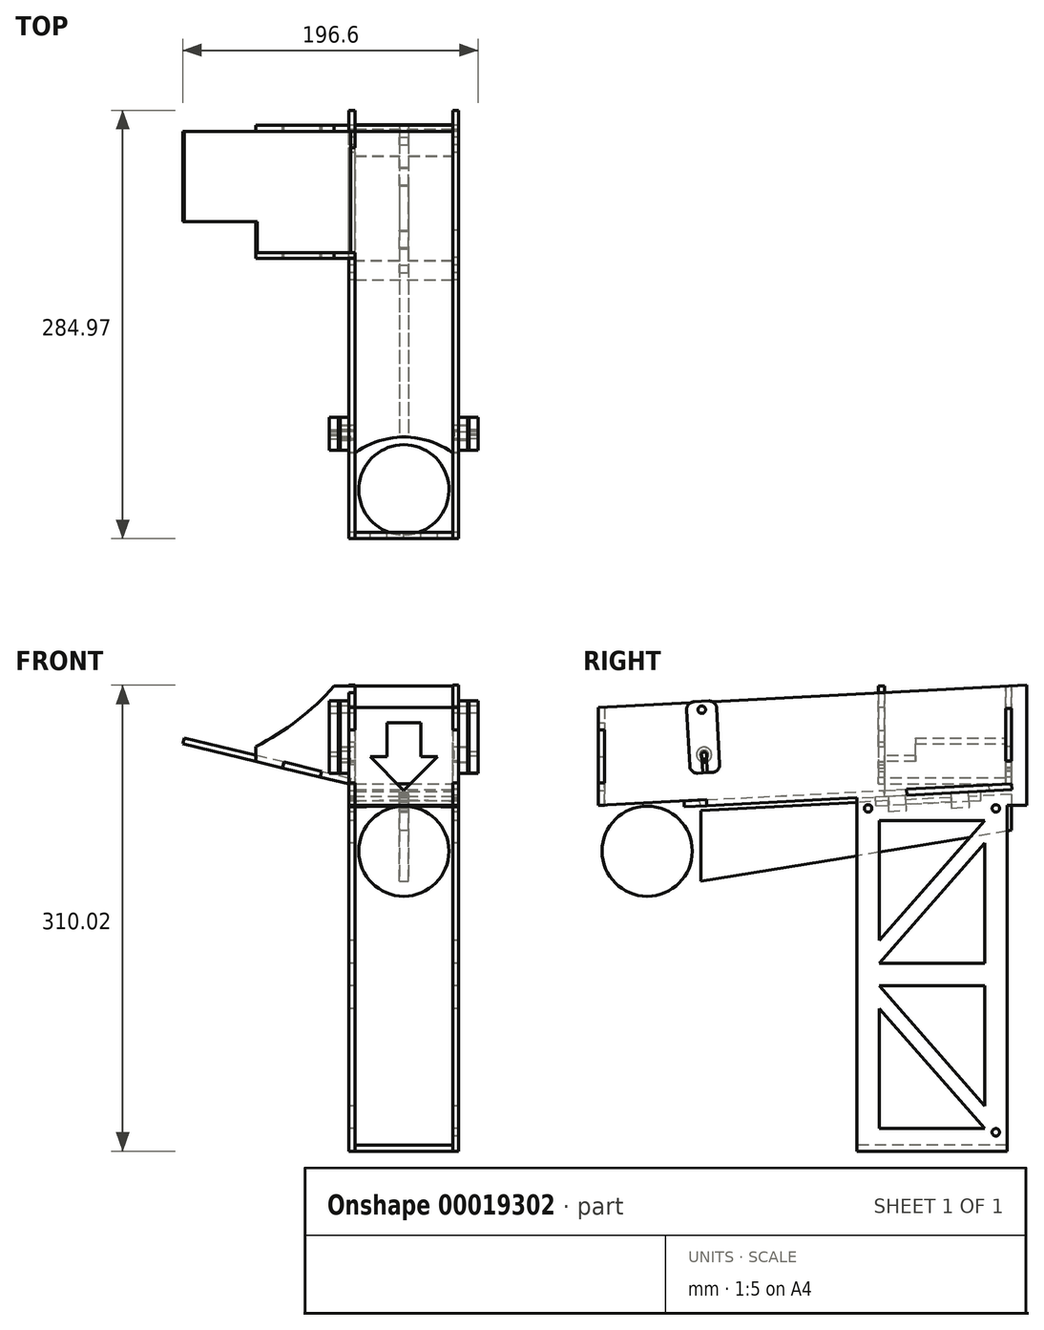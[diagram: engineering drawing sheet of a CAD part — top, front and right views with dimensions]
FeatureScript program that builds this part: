
annotation { "Feature Type Name" : "Feature", "Feature Type Description" : "" }
export const myFeature = defineFeature(function(context is Context, id is Id, definition is map)
    precondition{}
    {
        {
            var Q0;
            Q0=qCreatedBy(makeId("Right.planeOp"),FACE);
            var sketch = newSketch(context, id + "F0", { "sketchPlane" : qUnion([Q0])});
            skLineSegment(sketch, "E0", {"start": v(0, 0) * mm, "end": v(71.9, 3.77) * mm});
            skLineSegment(sketch, "E1", {"start": v(274.97, 79.5) * mm, "end": v(0, 65.09) * mm});
            skLineSegment(sketch, "E2", {"start": v(0, 65.09) * mm, "end": v(0, 50.09) * mm});
            skLineSegment(sketch, "E3.top", {"start": v(71.9, 0) * mm, "end": v(0, 0) * mm, "construction": true});
            skPoint(sketch, "E4.orphan", {"position": v(274.97, 14.41) * mm});
            skLineSegment(sketch, "E5", {"start": v(274.97, 14.41) * mm, "end": v(275.18, 10.42) * mm, "construction": true});
            skLineSegment(sketch, "E6", {"start": v(274.97, 79.5) * mm, "end": v(274.97, 14.41) * mm, "construction": true});
            skLineSegment(sketch, "E7", {"start": v(275.18, 10.42) * mm, "end": v(274.97, 14.41) * mm});
            skLineSegment(sketch, "E8", {"start": v(205.07, 10.75) * mm, "end": v(205.28, 6.75) * mm});
            skLineSegment(sketch, "E9", {"start": v(205.28, 6.75) * mm, "end": v(275.18, 10.42) * mm});
            skLineSegment(sketch, "E10.bottom", {"start": v(274.97, 64.5) * mm, "end": v(270.97, 64.5) * mm});
            skLineSegment(sketch, "E10.top", {"start": v(274.97, 29.5) * mm, "end": v(270.97, 29.5) * mm});
            skLineSegment(sketch, "E10.left", {"start": v(274.97, 64.5) * mm, "end": v(274.97, 29.5) * mm});
            skLineSegment(sketch, "E10.right", {"start": v(270.97, 64.5) * mm, "end": v(270.97, 29.5) * mm});
            skLineSegment(sketch, "E11", {"start": v(205.07, 10.75) * mm, "end": v(274.97, 14.41) * mm});
            skLineSegment(sketch, "E12", {"start": v(72.11, -0.23) * mm, "end": v(171.97, 5) * mm});
            skLineSegment(sketch, "E13", {"start": v(71.9, 3.77) * mm, "end": v(72.11, -0.23) * mm});
            skLineSegment(sketch, "E14.bottom", {"start": v(0, 50.09) * mm, "end": v(4, 50.09) * mm});
            skLineSegment(sketch, "E14.top", {"start": v(0, 15.09) * mm, "end": v(4, 15.09) * mm});
            skLineSegment(sketch, "E14.right", {"start": v(4, 50.09) * mm, "end": v(4, 15.09) * mm});
            skLineSegment(sketch, "E15.trimOffspring", {"start": v(0, 15.09) * mm, "end": v(0, 0) * mm});
            skLineSegment(sketch, "E16", {"start": v(171.97, 5) * mm, "end": v(171.97, -230) * mm});
            skLineSegment(sketch, "E17", {"start": v(171.97, -230) * mm, "end": v(271.97, -230) * mm});
            skLineSegment(sketch, "E18", {"start": v(284.97, 0) * mm, "end": v(284.97, 80.02) * mm});
            skLineSegment(sketch, "E19", {"start": v(284.97, 80.02) * mm, "end": v(274.97, 79.5) * mm});
            skLineSegment(sketch, "E20", {"start": v(284.97, 0) * mm, "end": v(271.97, 0) * mm});
            skLineSegment(sketch, "E21", {"start": v(271.97, 0) * mm, "end": v(271.97, -230) * mm});
            skLineSegment(sketch, "E22", {"start": v(186.97, -10) * mm, "end": v(256.97, -10) * mm});
            skLineSegment(sketch, "E23", {"start": v(256.97, -10) * mm, "end": v(186.97, -89.83) * mm});
            skLineSegment(sketch, "E24", {"start": v(186.97, -89.83) * mm, "end": v(186.97, -10) * mm});
            skLineSegment(sketch, "E25", {"start": v(186.97, -105) * mm, "end": v(256.97, -25.16) * mm});
            skLineSegment(sketch, "E26", {"start": v(256.97, -25.16) * mm, "end": v(256.97, -105) * mm});
            skLineSegment(sketch, "E27", {"start": v(256.97, -105) * mm, "end": v(186.97, -105) * mm});
            skLineSegment(sketch, "E28", {"start": v(186.97, -120) * mm, "end": v(256.97, -199.83) * mm});
            skLineSegment(sketch, "E29", {"start": v(256.97, -199.83) * mm, "end": v(256.97, -120) * mm});
            skLineSegment(sketch, "E30", {"start": v(256.97, -120) * mm, "end": v(186.97, -120) * mm});
            skLineSegment(sketch, "E31", {"start": v(186.97, -135.16) * mm, "end": v(256.97, -215) * mm});
            skLineSegment(sketch, "E32", {"start": v(256.97, -215) * mm, "end": v(186.97, -215) * mm});
            skLineSegment(sketch, "E33", {"start": v(186.97, -215) * mm, "end": v(186.97, -135.16) * mm});
            skCircle(sketch, "E34", {"center": v(70.33, 33.73) * mm, "radius": 5 * mm});
            skLineSegment(sketch, "E35", {"start": v(70.33, 33.73) * mm, "end": v(68.5, 68.68) * mm, "construction": true});
            skCircle(sketch, "E36", {"center": v(68.76, 63.69) * mm, "radius": 2.5 * mm});
            skCircle(sketch, "E37", {"center": v(179.47, -2) * mm, "radius": 2.5 * mm});
            skCircle(sketch, "E38", {"center": v(264.47, -2) * mm, "radius": 2.5 * mm});
            skCircle(sketch, "E39", {"center": v(264.47, -217.45) * mm, "radius": 2.5 * mm});
            skSolve(sketch);
        }
        {
            var Q0;
            Q0=qSketchRegion(id+"F0",true);
            extrude(context, id + "F1", {"entities" : qUnion([Q0]), "depth" : 4 * mm});
        }
        {
            var Q0;
            Q0=makeQuery(id+"F1.opExtrude","SWEPT_FACE",FACE,{"disambiguationData":[OSD([sQuery(id+"F0.wireOp",EDGE,"E0")])]});
            var sketch = newSketch(context, id + "F2", { "sketchPlane" : qUnion([Q0])});
            skLineSegment(sketch, "E40.top", {"start": v(4, -275.35) * mm, "end": v(0, -275.35) * mm});
            skLineSegment(sketch, "E40.left", {"start": v(4, -57) * mm, "end": v(4, -72) * mm});
            skLineSegment(sketch, "E40.right", {"start": v(-69, -57) * mm, "end": v(-69, -72) * mm});
            skLineSegment(sketch, "E41", {"start": v(4, -57) * mm, "end": v(0, -57) * mm});
            skLineSegment(sketch, "E42", {"start": v(-65, -275.35) * mm, "end": v(0, -275.35) * mm});
            skLineSegment(sketch, "E43", {"start": v(0, -72) * mm, "end": v(0, -205.35) * mm});
            skLineSegment(sketch, "E44.0", {"start": v(4, -72) * mm, "end": v(0, -72) * mm});
            skLineSegment(sketch, "E45.0", {"start": v(4, -205.35) * mm, "end": v(0, -205.35) * mm});
            skLineSegment(sketch, "E46", {"start": v(4, -205.35) * mm, "end": v(4, -275.35) * mm});
            skLineSegment(sketch, "E47", {"start": v(0, -275.35) * mm, "end": v(4, -275.35) * mm});
            skLineSegment(sketch, "E48.bottom", {"start": v(-69, -260.35) * mm, "end": v(-65, -260.35) * mm});
            skLineSegment(sketch, "E48.top", {"start": v(-69, -190.35) * mm, "end": v(-65, -190.35) * mm});
            skLineSegment(sketch, "E49", {"start": v(-65, -260.35) * mm, "end": v(-65, -275.35) * mm});
            skLineSegment(sketch, "E50", {"start": v(-69, -72) * mm, "end": v(-65, -72) * mm});
            skLineSegment(sketch, "E51", {"start": v(-65, -72) * mm, "end": v(-65, -190.35) * mm});
            skLineSegment(sketch, "E52.trimOffspring", {"start": v(-69, -190.35) * mm, "end": v(-69, -260.35) * mm});
            skArc(sketch, "E53", {"start": v(-65, -57) * mm, "mid": v(-32.5, -67.63) * mm, "end": v(0, -57) * mm});
            skLineSegment(sketch, "E54", {"start": v(-32.5, -57) * mm, "end": v(-32.5, -275.35) * mm, "construction": true});
            skLineSegment(sketch, "E55.trimOffspring", {"start": v(-65, -57) * mm, "end": v(-69, -57) * mm});
            skCircle(sketch, "E56", {"center": v(-32.5, -32.2) * mm, "radius": 30 * mm, "construction": true});
            skLineSegment(sketch, "E57", {"start": v(0, 0) * mm, "end": v(-69, 0) * mm, "construction": true});
            skLineSegment(sketch, "E58", {"start": v(-65, -57) * mm, "end": v(-65, 0) * mm, "construction": true});
            skSolve(sketch);
        }
        {
            var Q0;
            Q0=qSketchRegion(id+"F2",true);
            extrude(context, id + "F3", {"entities" : qUnion([Q0]), "depth" : 4 * mm});
        }
        {
            var Q0;
            Q0=makeQuery(id+"F3.opExtrude","SWEPT_FACE",FACE,{"disambiguationData":[OSD([sQuery(id+"F2.wireOp",EDGE,"E40.right")])]});
            var sketch = newSketch(context, id + "F4", { "sketchPlane" : qUnion([Q0])});
            skPoint(sketch, "E59.0.2.start.orphan", {"position": v(0, 65.09) * mm});
            skLineSegment(sketch, "E60.1", {"start": v(-274.97, 64.5) * mm, "end": v(-274.97, 29.5) * mm});
            skLineSegment(sketch, "E60.2", {"start": v(-274.97, 64.5) * mm, "end": v(-270.97, 64.5) * mm});
            skLineSegment(sketch, "E60.4", {"start": v(-274.97, 29.5) * mm, "end": v(-270.97, 29.5) * mm});
            skLineSegment(sketch, "E60.11", {"start": v(-190.3, 5.97) * mm, "end": v(-260.2, 9.63) * mm});
            skLineSegment(sketch, "E60.12", {"start": v(-260.2, 9.63) * mm, "end": v(-260, 13.63) * mm});
            skLineSegment(sketch, "E60.14", {"start": v(-190.3, 9.97) * mm, "end": v(-190.3, 5.97) * mm});
            skLineSegment(sketch, "E60.26", {"start": v(-72.11, -0.23) * mm, "end": v(-171.97, 5) * mm});
            skLineSegment(sketch, "E60.27", {"start": v(-71.9, 3.77) * mm, "end": v(-72.11, -0.23) * mm});
            skLineSegment(sketch, "E60.28", {"start": v(0, 0) * mm, "end": v(-71.9, 3.77) * mm});
            skLineSegment(sketch, "E60.29", {"start": v(0, 65.09) * mm, "end": v(0, 50.09) * mm});
            skLineSegment(sketch, "E61", {"start": v(-270.97, 64.5) * mm, "end": v(-270.97, 79.3) * mm});
            skLineSegment(sketch, "E62", {"start": v(-270.97, 29.5) * mm, "end": v(-270.97, 14.2) * mm});
            skLineSegment(sketch, "E63", {"start": v(-270.97, 14.2) * mm, "end": v(-260, 13.63) * mm});
            skLineSegment(sketch, "E64", {"start": v(-190.3, 75.06) * mm, "end": v(-190.3, 65.06) * mm});
            skLineSegment(sketch, "E65", {"start": v(0, 50.09) * mm, "end": v(-4, 50.09) * mm});
            skLineSegment(sketch, "E66", {"start": v(-4, 50.09) * mm, "end": v(-4, 15.09) * mm});
            skLineSegment(sketch, "E67", {"start": v(-4, 15.09) * mm, "end": v(0, 15.09) * mm});
            skLineSegment(sketch, "E68.trimOffspring", {"start": v(0, 15.09) * mm, "end": v(0, 0) * mm});
            skLineSegment(sketch, "E69.trimOffspring", {"start": v(0, 50.09) * mm, "end": v(0, 65.09) * mm});
            skPoint(sketch, "E59.0.0.start.orphan", {"position": v(0, 50.09) * mm});
            skLineSegment(sketch, "E70", {"start": v(-190.3, 65.06) * mm, "end": v(-186.3, 65.06) * mm});
            skLineSegment(sketch, "E71", {"start": v(-186.3, 65.06) * mm, "end": v(-186.3, 50.06) * mm});
            skLineSegment(sketch, "E72", {"start": v(-186.3, 50.06) * mm, "end": v(-190.3, 50.06) * mm});
            skLineSegment(sketch, "E73", {"start": v(-190.3, 42.06) * mm, "end": v(-186.3, 42.06) * mm});
            skLineSegment(sketch, "E74", {"start": v(-186.3, 42.06) * mm, "end": v(-186.3, 27.06) * mm});
            skLineSegment(sketch, "E75", {"start": v(-186.3, 27.06) * mm, "end": v(-190.3, 27.06) * mm});
            skLineSegment(sketch, "E76.trimOffspring", {"start": v(-190.3, 50.06) * mm, "end": v(-190.3, 42.06) * mm});
            skLineSegment(sketch, "E77.trimOffspring", {"start": v(-190.3, 27.06) * mm, "end": v(-190.3, 9.97) * mm});
            skLineSegment(sketch, "E78", {"start": v(-171.97, 5) * mm, "end": v(-171.97, -230) * mm});
            skLineSegment(sketch, "E79", {"start": v(-171.97, -230) * mm, "end": v(-271.97, -230) * mm});
            skLineSegment(sketch, "E80", {"start": v(-284.97, 0) * mm, "end": v(-284.97, 80.02) * mm});
            skLineSegment(sketch, "E81", {"start": v(-270.97, 79.3) * mm, "end": v(-284.97, 80.02) * mm});
            skLineSegment(sketch, "E82", {"start": v(0, 65.09) * mm, "end": v(-190.3, 75.06) * mm});
            skLineSegment(sketch, "E83", {"start": v(-271.97, 0) * mm, "end": v(-284.97, 0) * mm});
            skLineSegment(sketch, "E84.0", {"start": v(-186.97, -10) * mm, "end": v(-256.97, -10) * mm});
            skLineSegment(sketch, "E85.0", {"start": v(-186.97, -89.83) * mm, "end": v(-186.97, -10) * mm});
            skLineSegment(sketch, "E86.0", {"start": v(-256.97, -10) * mm, "end": v(-186.97, -89.83) * mm});
            skLineSegment(sketch, "E87.0", {"start": v(-186.97, -105) * mm, "end": v(-256.97, -25.16) * mm});
            skLineSegment(sketch, "E88.0", {"start": v(-256.97, -25.16) * mm, "end": v(-256.97, -105) * mm});
            skLineSegment(sketch, "E89.0", {"start": v(-256.97, -105) * mm, "end": v(-186.97, -105) * mm});
            skLineSegment(sketch, "E90.0", {"start": v(-256.97, -120) * mm, "end": v(-186.97, -120) * mm});
            skLineSegment(sketch, "E91.0", {"start": v(-256.97, -199.83) * mm, "end": v(-256.97, -120) * mm});
            skLineSegment(sketch, "E92.0", {"start": v(-186.97, -120) * mm, "end": v(-256.97, -199.83) * mm});
            skLineSegment(sketch, "E93.0", {"start": v(-186.97, -135.16) * mm, "end": v(-256.97, -215) * mm});
            skLineSegment(sketch, "E94.0", {"start": v(-186.97, -215) * mm, "end": v(-186.97, -135.16) * mm});
            skLineSegment(sketch, "E95.0", {"start": v(-256.97, -215) * mm, "end": v(-186.97, -215) * mm});
            skLineSegment(sketch, "E96", {"start": v(-271.97, -230) * mm, "end": v(-271.97, 0) * mm});
            skCircle(sketch, "E97.0", {"center": v(-70.33, 33.73) * mm, "radius": 5 * mm});
            skCircle(sketch, "E98.0", {"center": v(-68.76, 63.69) * mm, "radius": 2.5 * mm});
            skCircle(sketch, "E99.0", {"center": v(-179.47, -2) * mm, "radius": 2.5 * mm});
            skCircle(sketch, "E99.1", {"center": v(-264.47, -2) * mm, "radius": 2.5 * mm});
            skSolve(sketch);
        }
        {
            var Q0;
            Q0=qSketchRegion(id+"F4",true);
            extrude(context, id + "F5", {"entities" : qUnion([Q0]), "oppositeDirection" : true, "depth" : 4 * mm});
        }
        {
            var Q0;
            Q0=makeQuery(id+"F5.opExtrude","SWEPT_FACE",FACE,{"disambiguationData":[OSD([sQuery(id+"F4.wireOp",EDGE,"E66")])]});
            var sketch = newSketch(context, id + "F6", { "sketchPlane" : qUnion([Q0])});
            skLineSegment(sketch, "E100", {"start": v(-65, 65.09) * mm, "end": v(0, 65.09) * mm});
            skLineSegment(sketch, "E101", {"start": v(0, 65.09) * mm, "end": v(0, 50.09) * mm});
            skLineSegment(sketch, "E102", {"start": v(0, 50.09) * mm, "end": v(4, 50.09) * mm});
            skLineSegment(sketch, "E103", {"start": v(4, 50.09) * mm, "end": v(4, 15.09) * mm});
            skLineSegment(sketch, "E104", {"start": v(4, 15.09) * mm, "end": v(0, 15.09) * mm});
            skLineSegment(sketch, "E105", {"start": v(0, 15.09) * mm, "end": v(0, 0) * mm});
            skLineSegment(sketch, "E106", {"start": v(0, 0) * mm, "end": v(-65, 0) * mm});
            skLineSegment(sketch, "E107", {"start": v(-65, 0) * mm, "end": v(-65, 15.09) * mm});
            skLineSegment(sketch, "E108", {"start": v(-65, 15.09) * mm, "end": v(-69, 15.09) * mm});
            skLineSegment(sketch, "E109", {"start": v(-69, 15.09) * mm, "end": v(-69, 50.09) * mm});
            skLineSegment(sketch, "E110", {"start": v(-69, 50.09) * mm, "end": v(-65, 50.09) * mm});
            skLineSegment(sketch, "E111", {"start": v(-65, 50.09) * mm, "end": v(-65, 65.09) * mm});
            skLineSegment(sketch, "E112", {"start": v(-32.5, 55.09) * mm, "end": v(-43.75, 55.09) * mm});
            skLineSegment(sketch, "E113", {"start": v(-43.75, 55.09) * mm, "end": v(-43.75, 32.54) * mm});
            skLineSegment(sketch, "E114", {"start": v(-43.75, 32.54) * mm, "end": v(-55, 32.54) * mm});
            skLineSegment(sketch, "E115", {"start": v(-55, 32.54) * mm, "end": v(-32.5, 10) * mm});
            skLineSegment(sketch, "E116", {"start": v(-32.5, 55.09) * mm, "end": v(-32.5, 10) * mm, "construction": true});
            skLineSegment(sketch, "E117.0.MirrorCS", {"start": v(-32.5, 55.09) * mm, "end": v(-21.25, 55.09) * mm});
            skLineSegment(sketch, "E118.0.MirrorCS", {"start": v(-21.25, 55.09) * mm, "end": v(-21.25, 32.54) * mm});
            skLineSegment(sketch, "E119.0.MirrorCS", {"start": v(-21.25, 32.54) * mm, "end": v(-10, 32.54) * mm});
            skLineSegment(sketch, "E120.0.MirrorCS", {"start": v(-10, 32.54) * mm, "end": v(-32.5, 10) * mm});
            skLineSegment(sketch, "E121", {"start": v(-32.5, 55.09) * mm, "end": v(-32.5, 65.09) * mm, "construction": true});
            skPoint(sketch, "E122", {"position": v(-32.5, 32.54) * mm});
            skSolve(sketch);
        }
        {
            var Q0;
            Q0=qSketchRegion(id+"F6",true);
            extrude(context, id + "F7", {"entities" : qUnion([Q0]), "depth" : 4 * mm});
        }
        {
            var Q0;
            Q0=makeQuery(id+"F1.opExtrude","SWEPT_FACE",FACE,{"disambiguationData":[OSD([sQuery(id+"F0.wireOp",EDGE,"E10.right")])]});
            var sketch = newSketch(context, id + "F8", { "sketchPlane" : qUnion([Q0])});
            skLineSegment(sketch, "E123", {"start": v(65, 64.5) * mm, "end": v(65, 64.5) * mm});
            skLineSegment(sketch, "E124", {"start": v(65, 64.5) * mm, "end": v(69, 64.5) * mm});
            skLineSegment(sketch, "E125", {"start": v(69, 64.5) * mm, "end": v(69, 64.5) * mm});
            skLineSegment(sketch, "E126", {"start": v(131, 39.2) * mm, "end": v(131, 29.2) * mm});
            skLineSegment(sketch, "E127", {"start": v(131, 29.2) * mm, "end": v(113.71, 25.02) * mm});
            skLineSegment(sketch, "E128", {"start": v(69, 14.2) * mm, "end": v(69, 29.5) * mm});
            skLineSegment(sketch, "E129", {"start": v(69, 29.5) * mm, "end": v(65, 29.5) * mm});
            skLineSegment(sketch, "E130", {"start": v(65, 29.5) * mm, "end": v(65, 14.41) * mm});
            skLineSegment(sketch, "E131", {"start": v(65, 14.41) * mm, "end": v(0, 14.41) * mm});
            skLineSegment(sketch, "E132", {"start": v(0, 14.41) * mm, "end": v(0, 29.5) * mm});
            skLineSegment(sketch, "E133", {"start": v(0, 29.5) * mm, "end": v(-4, 29.5) * mm});
            skLineSegment(sketch, "E134", {"start": v(-4, 29.5) * mm, "end": v(-4, 64.5) * mm});
            skLineSegment(sketch, "E135", {"start": v(-4, 64.5) * mm, "end": v(0, 64.5) * mm});
            skLineSegment(sketch, "E136", {"start": v(0, 63.14) * mm, "end": v(0, 64.5) * mm});
            skLineSegment(sketch, "E137", {"start": v(69, 14.2) * mm, "end": v(131, 14.2) * mm, "construction": true});
            skLineSegment(sketch, "E138", {"start": v(131, 14.2) * mm, "end": v(131, 29.2) * mm, "construction": true});
            skArc(sketch, "E139", {"start": v(79, 79.3) * mm, "mid": v(103.1, 56.79) * mm, "end": v(131, 39.2) * mm});
            skLineSegment(sketch, "E140", {"start": v(88.44, 18.9) * mm, "end": v(87.5, 22.8) * mm});
            skLineSegment(sketch, "E141", {"start": v(87.5, 22.8) * mm, "end": v(112.77, 28.9) * mm});
            skLineSegment(sketch, "E142", {"start": v(112.77, 28.9) * mm, "end": v(113.71, 25.02) * mm});
            skLineSegment(sketch, "E143.trimOffspring", {"start": v(88.44, 18.9) * mm, "end": v(69, 14.2) * mm});
            skLineSegment(sketch, "E144", {"start": v(0, 64.5) * mm, "end": v(0, 79.3) * mm});
            skLineSegment(sketch, "E145", {"start": v(0, 79.3) * mm, "end": v(65, 79.3) * mm});
            skLineSegment(sketch, "E146", {"start": v(65, 79.3) * mm, "end": v(65, 64.5) * mm});
            skLineSegment(sketch, "E147", {"start": v(69, 64.5) * mm, "end": v(69, 79.3) * mm});
            skLineSegment(sketch, "E148", {"start": v(69, 79.3) * mm, "end": v(79, 79.3) * mm});
            skSolve(sketch);
        }
        {
            var Q0;
            Q0=qSketchRegion(id+"F8",true);
            extrude(context, id + "F9", {"entities" : qUnion([Q0]), "depth" : 4 * mm});
        }
        {
            var Q0;
            Q0=makeQuery(id+"F9.opExtrude","SWEPT_FACE",FACE,{"disambiguationData":[OSD([sQuery(id+"F8.wireOp",EDGE,"E127")])]});
            var sketch = newSketch(context, id + "F10", { "sketchPlane" : qUnion([Q0])});
            skLineSegment(sketch, "E149.top", {"start": v(-70.08, -190.3) * mm, "end": v(-90.08, -190.3) * mm});
            skLineSegment(sketch, "E149.right", {"start": v(-134.2, -210.97) * mm, "end": v(-134.2, -190.3) * mm});
            skLineSegment(sketch, "E150.bottom", {"start": v(-134.2, -210.97) * mm, "end": v(-184.2, -210.97) * mm});
            skLineSegment(sketch, "E150.top", {"start": v(-134.2, -270.97) * mm, "end": v(-184.2, -270.97) * mm});
            skLineSegment(sketch, "E150.right", {"start": v(-184.2, -210.97) * mm, "end": v(-184.2, -270.97) * mm});
            skLineSegment(sketch, "E151", {"start": v(-116.08, -270.97) * mm, "end": v(-116.08, -274.97) * mm});
            skLineSegment(sketch, "E152", {"start": v(-116.08, -274.97) * mm, "end": v(-90.08, -274.97) * mm});
            skLineSegment(sketch, "E153", {"start": v(-90.08, -274.97) * mm, "end": v(-90.08, -270.97) * mm});
            skLineSegment(sketch, "E154", {"start": v(-116.08, -190.3) * mm, "end": v(-116.08, -186.3) * mm});
            skLineSegment(sketch, "E155", {"start": v(-116.08, -186.3) * mm, "end": v(-90.08, -186.3) * mm});
            skLineSegment(sketch, "E156", {"start": v(-90.08, -186.3) * mm, "end": v(-90.08, -190.3) * mm});
            skLineSegment(sketch, "E157.trimOffspring", {"start": v(-116.08, -270.97) * mm, "end": v(-134.2, -270.97) * mm});
            skLineSegment(sketch, "E158.trimOffspring", {"start": v(-116.08, -190.3) * mm, "end": v(-134.2, -190.3) * mm});
            skLineSegment(sketch, "E159", {"start": v(-70.08, -270.82) * mm, "end": v(-70.08, -190.3) * mm});
            skLineSegment(sketch, "E160", {"start": v(-90.08, -270.97) * mm, "end": v(-70.08, -270.82) * mm});
            skSolve(sketch);
        }
        {
            var Q0;
            Q0=qSketchRegion(id+"F10",true);
            extrude(context, id + "F11", {"entities" : qUnion([Q0]), "oppositeDirection" : true, "depth" : 4 * mm});
        }
        {
            var Q0;
            Q0=makeQuery(id+"F11.opExtrude","SWEPT_FACE",FACE,{"disambiguationData":[OSD([sQuery(id+"F10.wireOp",EDGE,"E149.top")])]});
            var sketch = newSketch(context, id + "F12", { "sketchPlane" : qUnion([Q0])});
            skLineSegment(sketch, "E161.0", {"start": v(-131, 39.2) * mm, "end": v(-131, 29.2) * mm});
            skArc(sketch, "E161.1", {"start": v(-131, 39.2) * mm, "mid": v(-288.9, 351.56) * mm, "end": v(-131, 39.2) * mm});
            skLineSegment(sketch, "E162", {"start": v(-112.46, 28.83) * mm, "end": v(-113.4, 24.94) * mm});
            skLineSegment(sketch, "E163", {"start": v(-112.46, 28.83) * mm, "end": v(-87.19, 22.72) * mm});
            skLineSegment(sketch, "E164", {"start": v(-87.19, 22.72) * mm, "end": v(-88.13, 18.83) * mm});
            skLineSegment(sketch, "E165.trimOffspring", {"start": v(-113.4, 24.94) * mm, "end": v(-131, 29.2) * mm});
            skLineSegment(sketch, "E166.3", {"start": v(-65, 50.06) * mm, "end": v(-69, 50.06) * mm});
            skLineSegment(sketch, "E166.4", {"start": v(-69, 50.06) * mm, "end": v(-69, 42.06) * mm});
            skLineSegment(sketch, "E166.5", {"start": v(-65, 42.06) * mm, "end": v(-69, 42.06) * mm});
            skLineSegment(sketch, "E166.6", {"start": v(-65, 27.06) * mm, "end": v(-69, 27.06) * mm});
            skLineSegment(sketch, "E166.7", {"start": v(-69, 27.06) * mm, "end": v(-69, 14.2) * mm});
            skLineSegment(sketch, "E167.trimOffspring", {"start": v(-65, 65.06) * mm, "end": v(-65, 50.06) * mm});
            skLineSegment(sketch, "E168.trimOffspring", {"start": v(-65, 42.06) * mm, "end": v(-65, 27.06) * mm});
            skPoint(sketch, "E169.orphan", {"position": v(-69, 27.06) * mm});
            skLineSegment(sketch, "E170.0", {"start": v(-65, 65.06) * mm, "end": v(-69, 65.06) * mm});
            skLineSegment(sketch, "E170.1", {"start": v(-69, 75.06) * mm, "end": v(-69, 65.06) * mm});
            skLineSegment(sketch, "E171.0", {"start": v(-65, 79.3) * mm, "end": v(-79, 79.3) * mm});
            skArc(sketch, "E171.1", {"start": v(-79, 79.3) * mm, "mid": v(-103.1, 56.79) * mm, "end": v(-131, 39.2) * mm});
            skLineSegment(sketch, "E172.0", {"start": v(-65, 75.06) * mm, "end": v(-69, 75.06) * mm});
            skLineSegment(sketch, "E173", {"start": v(-65, 75.06) * mm, "end": v(-65, 79.3) * mm});
            skLineSegment(sketch, "E174", {"start": v(-88.13, 18.83) * mm, "end": v(-69, 14.2) * mm});
            skSolve(sketch);
        }
        {
            var Q0;
            Q0=qSketchRegion(id+"F12",true);
            extrude(context, id + "F13", {"entities" : qUnion([Q0]), "depth" : 4 * mm});
        }
        {
            var Q0;
            Q0=makeQuery(id+"F5.opExtrude","CAP_FACE",FACE,{"disambiguationData":[OSD([sQuery(id+"F4.wireOp",EDGE,"E59.0.1"),sQuery(id+"F4.wireOp",EDGE,"E60.0"),sQuery(id+"F4.wireOp",EDGE,"E60.1"),sQuery(id+"F4.wireOp",EDGE,"E60.2"),sQuery(id+"F4.wireOp",EDGE,"E60.4"),sQuery(id+"F4.wireOp",EDGE,"E60.5"),sQuery(id+"F4.wireOp",EDGE,"E60.6"),sQuery(id+"F4.wireOp",EDGE,"E60.7"),sQuery(id+"F4.wireOp",EDGE,"E60.8"),sQuery(id+"F4.wireOp",EDGE,"E60.9"),sQuery(id+"F4.wireOp",EDGE,"E60.10"),sQuery(id+"F4.wireOp",EDGE,"E60.11"),sQuery(id+"F4.wireOp",EDGE,"E60.12"),sQuery(id+"F4.wireOp",EDGE,"E60.14"),sQuery(id+"F4.wireOp",EDGE,"E60.15"),sQuery(id+"F4.wireOp",EDGE,"E60.16"),sQuery(id+"F4.wireOp",EDGE,"E60.17"),sQuery(id+"F4.wireOp",EDGE,"E60.18"),sQuery(id+"F4.wireOp",EDGE,"E60.19"),sQuery(id+"F4.wireOp",EDGE,"E60.20"),sQuery(id+"F4.wireOp",EDGE,"E60.21"),sQuery(id+"F4.wireOp",EDGE,"E60.22"),sQuery(id+"F4.wireOp",EDGE,"E60.23"),sQuery(id+"F4.wireOp",EDGE,"E60.24"),sQuery(id+"F4.wireOp",EDGE,"E60.25"),sQuery(id+"F4.wireOp",EDGE,"E60.26"),sQuery(id+"F4.wireOp",EDGE,"E60.27"),sQuery(id+"F4.wireOp",EDGE,"E60.28"),sQuery(id+"F4.wireOp",EDGE,"E61"),sQuery(id+"F4.wireOp",EDGE,"4ae15630-7873-4519-9142-a34cefbef92f"),sQuery(id+"F4.wireOp",EDGE,"E62"),sQuery(id+"F4.wireOp",EDGE,"E63"),sQuery(id+"F4.wireOp",EDGE,"E64"),sQuery(id+"F4.wireOp",EDGE,"ef37c952-c681-47c9-a026-029117f68ef9"),sQuery(id+"F4.wireOp",EDGE,"E65"),sQuery(id+"F4.wireOp",EDGE,"E66"),sQuery(id+"F4.wireOp",EDGE,"E67"),sQuery(id+"F4.wireOp",EDGE,"E68.trimOffspring"),sQuery(id+"F4.wireOp",EDGE,"E69.trimOffspring"),sQuery(id+"F4.wireOp",EDGE,"13c4a680-976b-49b9-a805-d054891e02a7.0"),sQuery(id+"F4.wireOp",EDGE,"13c4a680-976b-49b9-a805-d054891e02a7.1"),sQuery(id+"F4.wireOp",EDGE,"13c4a680-976b-49b9-a805-d054891e02a7.2"),sQuery(id+"F4.wireOp",EDGE,"13c4a680-976b-49b9-a805-d054891e02a7.3"),sQuery(id+"F4.wireOp",EDGE,"13c4a680-976b-49b9-a805-d054891e02a7.4"),sQuery(id+"F4.wireOp",EDGE,"13c4a680-976b-49b9-a805-d054891e02a7.5"),sQuery(id+"F4.wireOp",EDGE,"13c4a680-976b-49b9-a805-d054891e02a7.6"),sQuery(id+"F4.wireOp",EDGE,"13c4a680-976b-49b9-a805-d054891e02a7.7"),sQuery(id+"F4.wireOp",EDGE,"13c4a680-976b-49b9-a805-d054891e02a7.8"),sQuery(id+"F4.wireOp",EDGE,"13c4a680-976b-49b9-a805-d054891e02a7.9"),sQuery(id+"F4.wireOp",EDGE,"13c4a680-976b-49b9-a805-d054891e02a7.10"),sQuery(id+"F4.wireOp",EDGE,"13c4a680-976b-49b9-a805-d054891e02a7.11"),sQuery(id+"F4.wireOp",EDGE,"13c4a680-976b-49b9-a805-d054891e02a7.12"),sQuery(id+"F4.wireOp",EDGE,"13c4a680-976b-49b9-a805-d054891e02a7.13"),sQuery(id+"F4.wireOp",EDGE,"13c4a680-976b-49b9-a805-d054891e02a7.14"),sQuery(id+"F4.wireOp",EDGE,"13c4a680-976b-49b9-a805-d054891e02a7.15"),sQuery(id+"F4.wireOp",EDGE,"13c4a680-976b-49b9-a805-d054891e02a7.16"),sQuery(id+"F4.wireOp",EDGE,"13c4a680-976b-49b9-a805-d054891e02a7.17"),sQuery(id+"F4.wireOp",EDGE,"e613d2b2-fb36-4108-9489-dbbc835d8e5d")])],"isStart":true});
            var Q1;
            Q1=makeQuery(id+"F1.opExtrude","CAP_FACE",FACE,{"disambiguationData":[OSD([sQuery(id+"F0.wireOp",EDGE,"E0"),sQuery(id+"F0.wireOp",EDGE,"E1"),sQuery(id+"F0.wireOp",EDGE,"E2"),sQuery(id+"F0.wireOp",EDGE,"ecbc3025-46a1-4a21-8c2d-8ca136fd10ce"),sQuery(id+"F0.wireOp",EDGE,"2880ab20-c187-474d-a706-7b57105d8e94"),sQuery(id+"F0.wireOp",EDGE,"0fddf1f1-f98e-4ab2-9615-00887aecef17"),sQuery(id+"F0.wireOp",EDGE,"208d794d-60aa-41b5-82c0-fe83a0807e02"),sQuery(id+"F0.wireOp",EDGE,"ad43ec8c-1358-4201-866b-06ab896043ed.trimOffspring"),sQuery(id+"F0.wireOp",EDGE,"6aec1979-b0b5-4794-90ce-a0e7edb21cd4.trimOffspring"),sQuery(id+"F0.wireOp",EDGE,"781f0303-0491-42ec-a057-bea1d53d88dd"),sQuery(id+"F0.wireOp",EDGE,"9e0b33dc-0449-4d7b-81d1-819911022c4b"),sQuery(id+"F0.wireOp",EDGE,"4d3532ee-43e3-4ca5-8400-a337cc55de55"),sQuery(id+"F0.wireOp",EDGE,"b9521aba-0c13-404d-9ce5-fb4589b62adf"),sQuery(id+"F0.wireOp",EDGE,"1149e1d0-5c81-482d-91ef-e560cf3edfd4"),sQuery(id+"F0.wireOp",EDGE,"0e398b80-a194-43b6-abc4-8786c8afef94.0"),sQuery(id+"F0.wireOp",EDGE,"5c6cbf64-2606-42f1-a4f5-0fc4a52ef3d7.0"),sQuery(id+"F0.wireOp",EDGE,"4d74fcce-4ab5-4bb6-ac6c-11029cad5eb7.trimOffspring"),sQuery(id+"F0.wireOp",EDGE,"da44d0a2-5c99-41ba-b335-9bb7506599a5.trimOffspring"),sQuery(id+"F0.wireOp",EDGE,"3b17bb44-121f-48b3-8c56-af9687b41b5b.trimOffspring"),sQuery(id+"F0.wireOp",EDGE,"9b0d49c6-0c42-47df-9a44-ddff2b38050b.trimOffspring"),sQuery(id+"F0.wireOp",EDGE,"8bf3d40e-4444-4454-950e-a382101168c0.trimOffspring"),sQuery(id+"F0.wireOp",EDGE,"E7"),sQuery(id+"F0.wireOp",EDGE,"E8"),sQuery(id+"F0.wireOp",EDGE,"E9"),sQuery(id+"F0.wireOp",EDGE,"E10.bottom"),sQuery(id+"F0.wireOp",EDGE,"E10.top"),sQuery(id+"F0.wireOp",EDGE,"E10.left"),sQuery(id+"F0.wireOp",EDGE,"E10.right"),sQuery(id+"F0.wireOp",EDGE,"E11"),sQuery(id+"F0.wireOp",EDGE,"E12"),sQuery(id+"F0.wireOp",EDGE,"E13"),sQuery(id+"F0.wireOp",EDGE,"E14.bottom"),sQuery(id+"F0.wireOp",EDGE,"E14.top"),sQuery(id+"F0.wireOp",EDGE,"E14.right"),sQuery(id+"F0.wireOp",EDGE,"E15.trimOffspring"),sQuery(id+"F0.wireOp",EDGE,"67e9d4a4-6612-46a9-b78f-cee3d970e37c"),sQuery(id+"F0.wireOp",EDGE,"82a11beb-2c71-498b-902e-fc952377962e"),sQuery(id+"F0.wireOp",EDGE,"9588ac9d-bcda-421c-a4bd-41e23b2edbc5"),sQuery(id+"F0.wireOp",EDGE,"02b9a98e-32f5-40ef-8fb9-e26004df0a64"),sQuery(id+"F0.wireOp",EDGE,"dc889213-3576-4ee0-a069-f4b0c6e71711"),sQuery(id+"F0.wireOp",EDGE,"e56f485d-8124-4b69-9b85-b3169276481d"),sQuery(id+"F0.wireOp",EDGE,"0d52d249-b8f6-4065-a098-6e69c140fd1f"),sQuery(id+"F0.wireOp",EDGE,"d9fadca2-8baa-49a0-b5b0-133ea90d944e"),sQuery(id+"F0.wireOp",EDGE,"42b81d75-b9fb-4157-993e-05b2d4093cb1"),sQuery(id+"F0.wireOp",EDGE,"5574c320-a4d3-40aa-837f-de73dbd53ddf"),sQuery(id+"F0.wireOp",EDGE,"9af4e33b-ce38-4bea-8b0d-3dd6dd98b29b"),sQuery(id+"F0.wireOp",EDGE,"bf959ea4-5ed8-4200-886a-b8c140a79cc6"),sQuery(id+"F0.wireOp",EDGE,"ecbd6da1-b102-4117-82ba-1fdeef6d0258"),sQuery(id+"F0.wireOp",EDGE,"dd9c5bd0-b758-404d-b454-9f020d862811"),sQuery(id+"F0.wireOp",EDGE,"69b17388-3e88-4444-b724-01cea6cb24a0"),sQuery(id+"F0.wireOp",EDGE,"44668c6c-764a-4a30-8e2b-65c4e17f5acd"),sQuery(id+"F0.wireOp",EDGE,"f0342c91-f2e6-47d8-be2e-5402f316e99b"),sQuery(id+"F0.wireOp",EDGE,"6bac6410-c59d-44e9-91b3-d37824f8f91a"),sQuery(id+"F0.wireOp",EDGE,"0189b48e-bbd3-4051-9f87-7a468f3c420d"),sQuery(id+"F0.wireOp",EDGE,"97cedcc1-5329-4197-9c95-d0464c186a64"),sQuery(id+"F0.wireOp",EDGE,"484a21c0-b84d-43a3-9505-25d1f8d3e6e3.trimOffspring"),sQuery(id+"F0.wireOp",EDGE,"a70876d2-b323-4835-821d-e2388b2cd19f.trimOffspring"),sQuery(id+"F0.wireOp",EDGE,"5ce1ea04-273b-4c51-90df-2a8deb631d99.trimOffspring"),sQuery(id+"F0.wireOp",EDGE,"d057fd68-f9bd-48b3-b413-f94cdbbdc208.trimOffspring"),sQuery(id+"F0.wireOp",EDGE,"ccadc64e-e593-42f8-ba7e-2b0454f66ba6.trimOffspring"),sQuery(id+"F0.wireOp",EDGE,"10f1cc55-af96-418f-8562-3a6e91293355.trimOffspring"),sQuery(id+"F0.wireOp",EDGE,"9786bbd9-c922-453f-b92d-c32381db43c1")])],"isStart":false});
            cPlane(context, id + "F14", {"entities" : qUnion([Q0, Q1]), "cplaneType" : CPlaneType.MID_PLANE, "offset" : 150 * mm, "width" : 150 * mm, "height" : 150 * mm});
        }
        {
            var Q0;
            Q0=qCreatedBy(id+"F14.planeOp",FACE);
            var sketch = newSketch(context, id + "F15", { "sketchPlane" : qUnion([Q0])});
            skLineSegment(sketch, "E175", {"start": v(-2.44, -30.46) * mm, "end": v(-62.44, -30.46) * mm});
            skArc(sketch, "E176", {"start": v(-62.44, -30.46) * mm, "mid": v(-32.44, -60.46) * mm, "end": v(-2.44, -30.46) * mm});
            skArc(sketch, "E177", {"start": v(-2.44, -30.46) * mm, "mid": v(-32.44, -0.5) * mm, "end": v(-62.44, -30.46) * mm, "construction": true});
            skSolve(sketch);
        }
        {
            var Q0;
            Q0=qSketchRegion(id+"F15",true);
            var Q1;
            Q1=sQuery(id+"F15.wireOp",EDGE,"E175");
            revolve(context, id + "F16", {"entities" : qUnion([Q0]), "axis" : qUnion([Q1]), "revolveType" : RevolveType.FULL});
        }
        {
            var Q0;
            Q0=makeQuery(id+"F1.opExtrude","SWEPT_FACE",FACE,{"disambiguationData":[OSD([sQuery(id+"F0.wireOp",EDGE,"E17")])]});
            var sketch = newSketch(context, id + "F17", { "sketchPlane" : qUnion([Q0])});
            skLineSegment(sketch, "E178", {"start": v(-65, -271.97) * mm, "end": v(-65, -166.94) * mm});
            skLineSegment(sketch, "E179", {"start": v(-65, -171.97) * mm, "end": v(-65, -166.94) * mm});
            skLineSegment(sketch, "E180", {"start": v(-65, -171.97) * mm, "end": v(0, -171.97) * mm});
            skLineSegment(sketch, "E181", {"start": v(0, -166.94) * mm, "end": v(0, -171.97) * mm});
            skLineSegment(sketch, "E182", {"start": v(0, -166.94) * mm, "end": v(0, -271.97) * mm});
            skLineSegment(sketch, "E183", {"start": v(0, -271.97) * mm, "end": v(-65, -271.97) * mm});
            skSolve(sketch);
        }
        {
            var Q0;
            Q0=qSketchRegion(id+"F17",true);
            extrude(context, id + "F18", {"entities" : qUnion([Q0]), "oppositeDirection" : true, "depth" : 4 * mm});
        }
        {
            var Q0;
            Q0=makeQuery(id+"F5.opExtrude","CAP_FACE",FACE,{"disambiguationData":[OSD([sQuery(id+"F4.wireOp",EDGE,"E60.1"),sQuery(id+"F4.wireOp",EDGE,"E60.2"),sQuery(id+"F4.wireOp",EDGE,"E60.4"),sQuery(id+"F4.wireOp",EDGE,"E60.11"),sQuery(id+"F4.wireOp",EDGE,"E60.12"),sQuery(id+"F4.wireOp",EDGE,"E60.14"),sQuery(id+"F4.wireOp",EDGE,"E60.26"),sQuery(id+"F4.wireOp",EDGE,"E60.27"),sQuery(id+"F4.wireOp",EDGE,"E60.28"),sQuery(id+"F4.wireOp",EDGE,"E61"),sQuery(id+"F4.wireOp",EDGE,"E62"),sQuery(id+"F4.wireOp",EDGE,"E63"),sQuery(id+"F4.wireOp",EDGE,"E64"),sQuery(id+"F4.wireOp",EDGE,"E65"),sQuery(id+"F4.wireOp",EDGE,"E66"),sQuery(id+"F4.wireOp",EDGE,"E67"),sQuery(id+"F4.wireOp",EDGE,"E68.trimOffspring"),sQuery(id+"F4.wireOp",EDGE,"E69.trimOffspring"),sQuery(id+"F4.wireOp",EDGE,"E70"),sQuery(id+"F4.wireOp",EDGE,"E71"),sQuery(id+"F4.wireOp",EDGE,"E72"),sQuery(id+"F4.wireOp",EDGE,"E73"),sQuery(id+"F4.wireOp",EDGE,"E74"),sQuery(id+"F4.wireOp",EDGE,"E75"),sQuery(id+"F4.wireOp",EDGE,"E76.trimOffspring"),sQuery(id+"F4.wireOp",EDGE,"E77.trimOffspring"),sQuery(id+"F4.wireOp",EDGE,"E78"),sQuery(id+"F4.wireOp",EDGE,"E79"),sQuery(id+"F4.wireOp",EDGE,"E80"),sQuery(id+"F4.wireOp",EDGE,"E81"),sQuery(id+"F4.wireOp",EDGE,"E82"),sQuery(id+"F4.wireOp",EDGE,"E83"),sQuery(id+"F4.wireOp",EDGE,"E84.0"),sQuery(id+"F4.wireOp",EDGE,"E85.0"),sQuery(id+"F4.wireOp",EDGE,"E86.0"),sQuery(id+"F4.wireOp",EDGE,"E87.0"),sQuery(id+"F4.wireOp",EDGE,"E88.0"),sQuery(id+"F4.wireOp",EDGE,"E89.0"),sQuery(id+"F4.wireOp",EDGE,"E90.0"),sQuery(id+"F4.wireOp",EDGE,"E91.0"),sQuery(id+"F4.wireOp",EDGE,"E92.0"),sQuery(id+"F4.wireOp",EDGE,"E93.0"),sQuery(id+"F4.wireOp",EDGE,"E94.0"),sQuery(id+"F4.wireOp",EDGE,"E95.0"),sQuery(id+"F4.wireOp",EDGE,"E96"),sQuery(id+"F4.wireOp",EDGE,"E97.0")])],"isStart":false});
            var sketch = newSketch(context, id + "F19", { "sketchPlane" : qUnion([Q0])});
            skCircle(sketch, "E184.0", {"center": v(70.33, 33.73) * mm, "radius": 5 * mm});
            skCircle(sketch, "E185", {"center": v(70.33, 33.73) * mm, "radius": 2.5 * mm});
            skSolve(sketch);
        }
        {
            var Q0;
            Q0=qSketchRegion(id+"F19",true);
            extrude(context, id + "F20", {"entities" : qUnion([Q0]), "oppositeDirection" : true, "depth" : 10 * mm});
        }
        {
            var Q0;
            Q0=makeQuery(id+"F20.opExtrude","SWEPT_BODY",BODY,{"disambiguationData":[OSD([sQuery(id+"F19.wireOp",EDGE,"E184.0"),sQuery(id+"F19.wireOp",EDGE,"E185")])]});
            var Q1;
            Q1=qCreatedBy(id+"F14.planeOp",FACE);
            mirror(context, id + "F21", {"entities" : qUnion([Q0]), "mirrorPlane" : qUnion([Q1])});
        }
        {
            var Q0;
            Q0=makeQuery(id+"F21.opPattern","COPY",FACE,{"derivedFrom":makeQuery(id+"F20.opExtrude","CAP_FACE",FACE,{"disambiguationData":[OSD([sQuery(id+"F19.wireOp",EDGE,"E184.0"),sQuery(id+"F19.wireOp",EDGE,"E185")])],"isStart":false}),"instanceName":"1"});
            var sketch = newSketch(context, id + "F22", { "sketchPlane" : qUnion([Q0])});
            skCircle(sketch, "E186.0", {"center": v(70.33, 33.73) * mm, "radius": 2.5 * mm});
            skSolve(sketch);
        }
        {
            var Q0;
            Q0=qSketchRegion(id+"F22",true);
            extrude(context, id + "F23", {"entities" : qUnion([Q0]), "oppositeDirection" : true, "depth" : 9 * mm});
        }
        {
            var Q0;
            Q0=makeQuery(id+"F23.opExtrude","CAP_FACE",FACE,{"disambiguationData":[OSD([sQuery(id+"F22.wireOp",EDGE,"E186.0")])],"isStart":true});
            var sketch = newSketch(context, id + "F24", { "sketchPlane" : qUnion([Q0])});
            skCircle(sketch, "E187", {"center": v(70.33, 33.73) * mm, "radius": 3 * mm});
            skSolve(sketch);
        }
        {
            var Q0;
            Q0=qSketchRegion(id+"F24",true);
            extrude(context, id + "F25", {"entities" : qUnion([Q0]), "operationType" : NewBodyOperationType.ADD, "depth" : 1 * mm});
        }
        {
            var Q0;
            Q0=makeQuery(id+"F21.opPattern","COPY",FACE,{"derivedFrom":makeQuery(id+"F20.opExtrude","CAP_FACE",FACE,{"disambiguationData":[OSD([sQuery(id+"F19.wireOp",EDGE,"E184.0"),sQuery(id+"F19.wireOp",EDGE,"E185")])],"isStart":false}),"instanceName":"1"});
            var sketch = newSketch(context, id + "F26", { "sketchPlane" : qUnion([Q0])});
            skLineSegment(sketch, "E188", {"start": v(60.97, 21.22) * mm, "end": v(58.49, 68.66) * mm});
            skLineSegment(sketch, "E189", {"start": v(80.95, 22.27) * mm, "end": v(60.97, 21.22) * mm});
            skLineSegment(sketch, "E190", {"start": v(67.87, 80.66) * mm, "end": v(70.96, 21.74) * mm, "construction": true});
            skPoint(sketch, "E191", {"position": v(70.33, 33.73) * mm});
            skLineSegment(sketch, "E192", {"start": v(63.48, 68.92) * mm, "end": v(78.46, 69.7) * mm});
            skLineSegment(sketch, "E193", {"start": v(78.13, 76) * mm, "end": v(78.46, 69.7) * mm, "construction": true});
            skLineSegment(sketch, "E194", {"start": v(78.46, 69.7) * mm, "end": v(80.95, 22.27) * mm});
            skCircle(sketch, "E195.0", {"center": v(70.33, 33.73) * mm, "radius": 5 * mm});
            skCircle(sketch, "E196", {"center": v(68.76, 63.69) * mm, "radius": 2.5 * mm});
            skLineSegment(sketch, "E197", {"start": v(58.49, 68.66) * mm, "end": v(63.48, 68.92) * mm});
            skSolve(sketch);
        }
        {
            var Q0;
            Q0=qSketchRegion(id+"F26",true);
            var Q1;
            Q1=qConstructionFilter(qBodyType(qCreatedBy(id+"F26",EDGE),BodyType.WIRE),ConstructionObject.NO);
            extrude(context, id + "F27", {"entities" : qUnion([Q0]), "surfaceEntities" : qUnion([Q1]), "oppositeDirection" : true, "depth" : 6 * mm});
        }
        {
            var Q0;
            Q0=makeQuery(id+"F27.opExtrude","SWEPT_EDGE",EDGE,{"disambiguationData":[OSD([sQuery(id+"F26.wireOp",EDGE,"E188"),sQuery(id+"F26.wireOp",EDGE,"E189")])]});
            var Q1;
            Q1=makeQuery(id+"F27.opExtrude","SWEPT_EDGE",EDGE,{"disambiguationData":[OSD([sQuery(id+"F26.wireOp",EDGE,"E189"),sQuery(id+"F26.wireOp",EDGE,"E194")])]});
            var Q2;
            Q2=makeQuery(id+"F27.opExtrude","SWEPT_EDGE",EDGE,{"disambiguationData":[OSD([sQuery(id+"F26.wireOp",EDGE,"E188"),sQuery(id+"F26.wireOp",EDGE,"38e441c7-f443-4d43-8b20-621526334bb9")])]});
            var Q3;
            Q3=makeQuery(id+"F27.opExtrude","SWEPT_EDGE",EDGE,{"disambiguationData":[OSD([sQuery(id+"F26.wireOp",EDGE,"E192"),sQuery(id+"F26.wireOp",EDGE,"E194")])]});
            fillet(context, id + "F28", {"entities" : qUnion([Q0, Q1, Q2, Q3]), "radius" : 5 * mm, "tangentPropagation" : true, "allowEdgeOverflow" : false});
        }
        {
            var Q0;
            Q0=makeQuery(id+"F27.opExtrude","CAP_FACE",FACE,{"disambiguationData":[OSD([sQuery(id+"F26.wireOp",EDGE,"E188"),sQuery(id+"F26.wireOp",EDGE,"38e441c7-f443-4d43-8b20-621526334bb9"),sQuery(id+"F26.wireOp",EDGE,"0add7988-c66c-4db9-8692-c3cffa355961"),sQuery(id+"F26.wireOp",EDGE,"E189"),sQuery(id+"F26.wireOp",EDGE,"91f00665-3601-4223-a845-a2353cb52a70"),sQuery(id+"F26.wireOp",EDGE,"531e93db-a306-41ea-b19c-ad4d79627dc1"),sQuery(id+"F26.wireOp",EDGE,"E192"),sQuery(id+"F26.wireOp",EDGE,"E194"),sQuery(id+"F26.wireOp",EDGE,"E195.0"),sQuery(id+"F26.wireOp",EDGE,"E196")])],"isStart":true});
            var sketch = newSketch(context, id + "F29", { "sketchPlane" : qUnion([Q0])});
            skArc(sketch, "E198.0", {"start": v(71.97, 31.21) * mm, "mid": v(70.17, 36.72) * mm, "end": v(68.97, 31.05) * mm});
            skCircle(sketch, "E198.1", {"center": v(68.76, 63.69) * mm, "radius": 2.5 * mm});
            skLineSegment(sketch, "E199", {"start": v(58.75, 63.66) * mm, "end": v(60.97, 21.22) * mm});
            skLineSegment(sketch, "E200", {"start": v(60.97, 21.22) * mm, "end": v(69.46, 21.67) * mm});
            skLineSegment(sketch, "E201", {"start": v(80.95, 22.27) * mm, "end": v(78.72, 64.7) * mm});
            skLineSegment(sketch, "E202", {"start": v(73.47, 69.44) * mm, "end": v(63.48, 68.92) * mm});
            skLineSegment(sketch, "E203", {"start": v(72.46, 21.82) * mm, "end": v(71.97, 31.21) * mm});
            skLineSegment(sketch, "E204", {"start": v(69.46, 21.67) * mm, "end": v(68.97, 31.05) * mm});
            skLineSegment(sketch, "E205", {"start": v(68.97, 31.05) * mm, "end": v(71.97, 31.21) * mm, "construction": true});
            skLineSegment(sketch, "E206.trimOffspring", {"start": v(72.46, 21.82) * mm, "end": v(80.95, 22.27) * mm});
            skArc(sketch, "E207", {"start": v(63.48, 68.92) * mm, "mid": v(60.03, 67.27) * mm, "end": v(58.75, 63.66) * mm});
            skArc(sketch, "E208", {"start": v(78.72, 64.7) * mm, "mid": v(77.07, 68.16) * mm, "end": v(73.47, 69.44) * mm});
            skSolve(sketch);
        }
        {
            var Q0;
            Q0=qSketchRegion(id+"F29",true);
            extrude(context, id + "F30", {"entities" : qUnion([Q0]), "depth" : 1 * mm});
        }
        {
            var Q0;
            Q0=makeQuery(id+"F30.opExtrude","CAP_FACE",FACE,{"disambiguationData":[OSD([sQuery(id+"F29.wireOp",EDGE,"E198.0"),sQuery(id+"F29.wireOp",EDGE,"E198.1"),sQuery(id+"F29.wireOp",EDGE,"E199"),sQuery(id+"F29.wireOp",EDGE,"E200"),sQuery(id+"F29.wireOp",EDGE,"E201"),sQuery(id+"F29.wireOp",EDGE,"E202"),sQuery(id+"F29.wireOp",EDGE,"E203"),sQuery(id+"F29.wireOp",EDGE,"E204"),sQuery(id+"F29.wireOp",EDGE,"E206.trimOffspring")])],"isStart":false});
            var sketch = newSketch(context, id + "F31", { "sketchPlane" : qUnion([Q0])});
            skLineSegment(sketch, "E209.0.1", {"start": v(58.75, 63.66) * mm, "end": v(60.97, 21.22) * mm});
            skLineSegment(sketch, "E209.0.2", {"start": v(60.97, 21.22) * mm, "end": v(69.46, 21.67) * mm});
            skLineSegment(sketch, "E209.0.6", {"start": v(72.46, 21.82) * mm, "end": v(80.95, 22.27) * mm});
            skLineSegment(sketch, "E209.0.7", {"start": v(80.95, 22.27) * mm, "end": v(78.72, 64.7) * mm});
            skCircle(sketch, "E210.0", {"center": v(68.76, 63.69) * mm, "radius": 2.5 * mm});
            skArc(sketch, "E211", {"start": v(71.88, 32.9) * mm, "mid": v(70.24, 35.47) * mm, "end": v(68.88, 32.75) * mm});
            skLineSegment(sketch, "E212", {"start": v(69.46, 21.67) * mm, "end": v(68.88, 32.75) * mm});
            skLineSegment(sketch, "E213", {"start": v(72.46, 21.82) * mm, "end": v(71.88, 32.9) * mm});
            skLineSegment(sketch, "E214", {"start": v(63.48, 68.92) * mm, "end": v(73.47, 69.44) * mm});
            skArc(sketch, "E215", {"start": v(63.48, 68.92) * mm, "mid": v(60.03, 67.27) * mm, "end": v(58.75, 63.66) * mm});
            skArc(sketch, "E216", {"start": v(78.72, 64.7) * mm, "mid": v(77.07, 68.16) * mm, "end": v(73.47, 69.44) * mm});
            skSolve(sketch);
        }
        {
            var Q0;
            Q0=qSketchRegion(id+"F31",true);
            extrude(context, id + "F32", {"entities" : qUnion([Q0]), "depth" : 6 * mm});
        }
        {
            var Q0;
            Q0=makeQuery(id+"F32.opExtrude","SWEPT_EDGE",EDGE,{"disambiguationData":[OSD([sQuery(id+"F31.wireOp",EDGE,"E209.0.1"),sQuery(id+"F31.wireOp",EDGE,"E209.0.2")])]});
            var Q1;
            Q1=makeQuery(id+"F30.opExtrude","SWEPT_EDGE",EDGE,{"disambiguationData":[OSD([sQuery(id+"F29.wireOp",EDGE,"E199"),sQuery(id+"F29.wireOp",EDGE,"E200")])]});
            var Q2;
            Q2=makeQuery(id+"F30.opExtrude","SWEPT_EDGE",EDGE,{"disambiguationData":[OSD([sQuery(id+"F29.wireOp",EDGE,"E201"),sQuery(id+"F29.wireOp",EDGE,"E206.trimOffspring")])]});
            var Q3;
            Q3=makeQuery(id+"F32.opExtrude","SWEPT_EDGE",EDGE,{"disambiguationData":[OSD([sQuery(id+"F31.wireOp",EDGE,"E209.0.6"),sQuery(id+"F31.wireOp",EDGE,"E209.0.7")])]});
            var Q4;
            Q4=makeQuery(id+"F30.opExtrude","SWEPT_EDGE",EDGE,{"disambiguationData":[OSD([sQuery(id+"F29.wireOp",EDGE,"E201"),sQuery(id+"F29.wireOp",EDGE,"E202")])]});
            var Q5;
            Q5=makeQuery(id+"F32.opExtrude","SWEPT_EDGE",EDGE,{"disambiguationData":[OSD([sQuery(id+"F31.wireOp",EDGE,"E209.0.0"),sQuery(id+"F31.wireOp",EDGE,"E209.0.7")])]});
            var Q6;
            Q6=makeQuery(id+"F30.opExtrude","SWEPT_EDGE",EDGE,{"disambiguationData":[OSD([sQuery(id+"F29.wireOp",EDGE,"E199"),sQuery(id+"F29.wireOp",EDGE,"E202")])]});
            var Q7;
            Q7=makeQuery(id+"F32.opExtrude","SWEPT_EDGE",EDGE,{"disambiguationData":[OSD([sQuery(id+"F31.wireOp",EDGE,"E209.0.0"),sQuery(id+"F31.wireOp",EDGE,"E209.0.1")])]});
            fillet(context, id + "F33", {"entities" : qUnion([Q0, Q1, Q2, Q3, Q4, Q5, Q6, Q7]), "radius" : 5 * mm, "tangentPropagation" : true, "allowEdgeOverflow" : false});
        }
        {
            var Q0;
            Q0=makeQuery(id+"F27.opExtrude","SWEPT_BODY",BODY,{"disambiguationData":[OSD([sQuery(id+"F26.wireOp",EDGE,"E188"),sQuery(id+"F26.wireOp",EDGE,"38e441c7-f443-4d43-8b20-621526334bb9"),sQuery(id+"F26.wireOp",EDGE,"0add7988-c66c-4db9-8692-c3cffa355961"),sQuery(id+"F26.wireOp",EDGE,"E189"),sQuery(id+"F26.wireOp",EDGE,"91f00665-3601-4223-a845-a2353cb52a70"),sQuery(id+"F26.wireOp",EDGE,"531e93db-a306-41ea-b19c-ad4d79627dc1"),sQuery(id+"F26.wireOp",EDGE,"E192"),sQuery(id+"F26.wireOp",EDGE,"E194"),sQuery(id+"F26.wireOp",EDGE,"E195.0")])]});
            var Q1;
            Q1=makeQuery(id+"F23.opExtrude","SWEPT_BODY",BODY,{"disambiguationData":[OSD([sQuery(id+"F22.wireOp",EDGE,"E186.0")])]});
            var Q2;
            Q2=makeQuery(id+"F32.opExtrude","SWEPT_BODY",BODY,{"disambiguationData":[OSD([sQuery(id+"F31.wireOp",EDGE,"E209.0.0"),sQuery(id+"F31.wireOp",EDGE,"E209.0.1"),sQuery(id+"F31.wireOp",EDGE,"E209.0.2"),sQuery(id+"F31.wireOp",EDGE,"E209.0.6"),sQuery(id+"F31.wireOp",EDGE,"E209.0.7"),sQuery(id+"F31.wireOp",EDGE,"E210.0"),sQuery(id+"F31.wireOp",EDGE,"E211"),sQuery(id+"F31.wireOp",EDGE,"E212"),sQuery(id+"F31.wireOp",EDGE,"E213")])]});
            var Q3;
            Q3=makeQuery(id+"F30.opExtrude","SWEPT_BODY",BODY,{"disambiguationData":[OSD([sQuery(id+"F29.wireOp",EDGE,"E198.0"),sQuery(id+"F29.wireOp",EDGE,"E198.1"),sQuery(id+"F29.wireOp",EDGE,"E199"),sQuery(id+"F29.wireOp",EDGE,"E200"),sQuery(id+"F29.wireOp",EDGE,"E201"),sQuery(id+"F29.wireOp",EDGE,"E202"),sQuery(id+"F29.wireOp",EDGE,"E203"),sQuery(id+"F29.wireOp",EDGE,"E204"),sQuery(id+"F29.wireOp",EDGE,"E206.trimOffspring")])]});
            var Q4;
            Q4=qCreatedBy(id+"F14.planeOp",FACE);
            mirror(context, id + "F34", {"entities" : qUnion([Q0, Q1, Q2, Q3]), "mirrorPlane" : qUnion([Q4])});
        }
        {
            var Q0;
            Q0=qCreatedBy(id+"F14.planeOp",FACE);
            var sketch = newSketch(context, id + "F35", { "sketchPlane" : qUnion([Q0])});
            skLineSegment(sketch, "E217", {"start": v(-68.19, -0.43) * mm, "end": v(-192.47, 6.08) * mm, "construction": true});
            skLineSegment(sketch, "E218", {"start": v(-274.97, 10.4) * mm, "end": v(-274.97, -16.6) * mm});
            skLineSegment(sketch, "E219", {"start": v(-274.97, -16.6) * mm, "end": v(-68.19, -50.43) * mm});
            skLineSegment(sketch, "E220", {"start": v(-68.19, -50.43) * mm, "end": v(-68.19, -0.43) * mm});
            skCircle(sketch, "E221.0", {"center": v(-179.47, -2) * mm, "radius": 2.5 * mm});
            skCircle(sketch, "E222.0", {"center": v(-264.47, -2) * mm, "radius": 2.5 * mm});
            skLineSegment(sketch, "E223", {"start": v(-192.47, 6.08) * mm, "end": v(-193, -3.9) * mm});
            skLineSegment(sketch, "E224", {"start": v(-193, -3.9) * mm, "end": v(-204.97, -3.28) * mm});
            skLineSegment(sketch, "E225", {"start": v(-204.97, -3.28) * mm, "end": v(-204.45, 6.7) * mm});
            skLineSegment(sketch, "E226", {"start": v(-234.4, 8.28) * mm, "end": v(-234.93, -1.7) * mm});
            skLineSegment(sketch, "E227", {"start": v(-234.93, -1.7) * mm, "end": v(-246.92, -1.08) * mm});
            skLineSegment(sketch, "E228", {"start": v(-246.92, -1.08) * mm, "end": v(-246.4, 8.9) * mm});
            skLineSegment(sketch, "E229.trimOffspring", {"start": v(-204.45, 6.7) * mm, "end": v(-234.4, 8.28) * mm, "construction": true});
            skLineSegment(sketch, "E230.trimOffspring", {"start": v(-246.4, 8.9) * mm, "end": v(-274.97, 10.4) * mm, "construction": true});
            skLineSegment(sketch, "E231", {"start": v(-274.97, 7.4) * mm, "end": v(-246.55, 5.91) * mm});
            skLineSegment(sketch, "E232.trimOffspring", {"start": v(-192.62, 3.09) * mm, "end": v(-68.19, -3.44) * mm});
            skLineSegment(sketch, "E233.trimOffspring", {"start": v(-234.57, 5.28) * mm, "end": v(-204.6, 3.71) * mm});
            skSolve(sketch);
        }
        {
            var Q0;
            Q0=qSketchRegion(id+"F35",true);
            extrude(context, id + "F36", {"entities" : qUnion([Q0]), "depth" : 3 * mm, "hasSecondDirection" : true, "secondDirectionOppositeDirection" : true, "secondDirectionDepth" : 3 * mm});
        }
        {
            var Q0;
            Q0=makeQuery(id+"F3.opExtrude","CAP_FACE",FACE,{"disambiguationData":[OSD([sQuery(id+"F2.wireOp",EDGE,"E40.left"),sQuery(id+"F2.wireOp",EDGE,"E40.right"),sQuery(id+"F2.wireOp",EDGE,"E41"),sQuery(id+"F2.wireOp",EDGE,"E42"),sQuery(id+"F2.wireOp",EDGE,"E44.0"),sQuery(id+"F2.wireOp",EDGE,"E43"),sQuery(id+"F2.wireOp",EDGE,"E45.0"),sQuery(id+"F2.wireOp",EDGE,"E47"),sQuery(id+"F2.wireOp",EDGE,"E46"),sQuery(id+"F2.wireOp",EDGE,"E48.bottom"),sQuery(id+"F2.wireOp",EDGE,"E48.top"),sQuery(id+"F2.wireOp",EDGE,"E49"),sQuery(id+"F2.wireOp",EDGE,"E50"),sQuery(id+"F2.wireOp",EDGE,"E51"),sQuery(id+"F2.wireOp",EDGE,"E52.trimOffspring"),sQuery(id+"F2.wireOp",EDGE,"E53"),sQuery(id+"F2.wireOp",EDGE,"E55.trimOffspring")])],"isStart":false});
            var sketch = newSketch(context, id + "F37", { "sketchPlane" : qUnion([Q0])});
            skLineSegment(sketch, "E234", {"start": v(0, -184.52) * mm, "end": v(-29.37, -184.52) * mm});
            skLineSegment(sketch, "E235", {"start": v(-65, -184.52) * mm, "end": v(-65, -254.52) * mm});
            skLineSegment(sketch, "E236", {"start": v(-65, -254.52) * mm, "end": v(-35.62, -254.52) * mm});
            skLineSegment(sketch, "E237", {"start": v(0, -184.52) * mm, "end": v(0, -254.52) * mm});
            skLineSegment(sketch, "E238", {"start": v(-29.37, -184.52) * mm, "end": v(-29.37, -193.3) * mm});
            skLineSegment(sketch, "E239", {"start": v(-35.62, -193.3) * mm, "end": v(-35.62, -184.52) * mm});
            skLineSegment(sketch, "E240", {"start": v(-35.62, -235.03) * mm, "end": v(-35.62, -204.53) * mm});
            skLineSegment(sketch, "E241", {"start": v(-29.37, -204.53) * mm, "end": v(-29.37, -235.03) * mm});
            skLineSegment(sketch, "E242", {"start": v(-29.37, -254.52) * mm, "end": v(-29.37, -246.47) * mm});
            skLineSegment(sketch, "E243", {"start": v(-35.62, -246.47) * mm, "end": v(-35.62, -254.52) * mm});
            skLineSegment(sketch, "E244.trimOffspring", {"start": v(-29.37, -254.52) * mm, "end": v(0, -254.52) * mm});
            skLineSegment(sketch, "E245.trimOffspring", {"start": v(-35.62, -184.52) * mm, "end": v(-65, -184.52) * mm});
            skLineSegment(sketch, "E246", {"start": v(-35.62, -246.47) * mm, "end": v(-29.37, -246.47) * mm});
            skLineSegment(sketch, "E247", {"start": v(-35.62, -235.03) * mm, "end": v(-29.37, -235.03) * mm});
            skLineSegment(sketch, "E248", {"start": v(-35.62, -204.53) * mm, "end": v(-29.37, -204.53) * mm});
            skLineSegment(sketch, "E249", {"start": v(-35.62, -193.3) * mm, "end": v(-29.37, -193.3) * mm});
            skSolve(sketch);
        }
        {
            var Q0;
            Q0=qSketchRegion(id+"F37",true);
            extrude(context, id + "F38", {"entities" : qUnion([Q0]), "depth" : 6 * mm});
        }
    });
